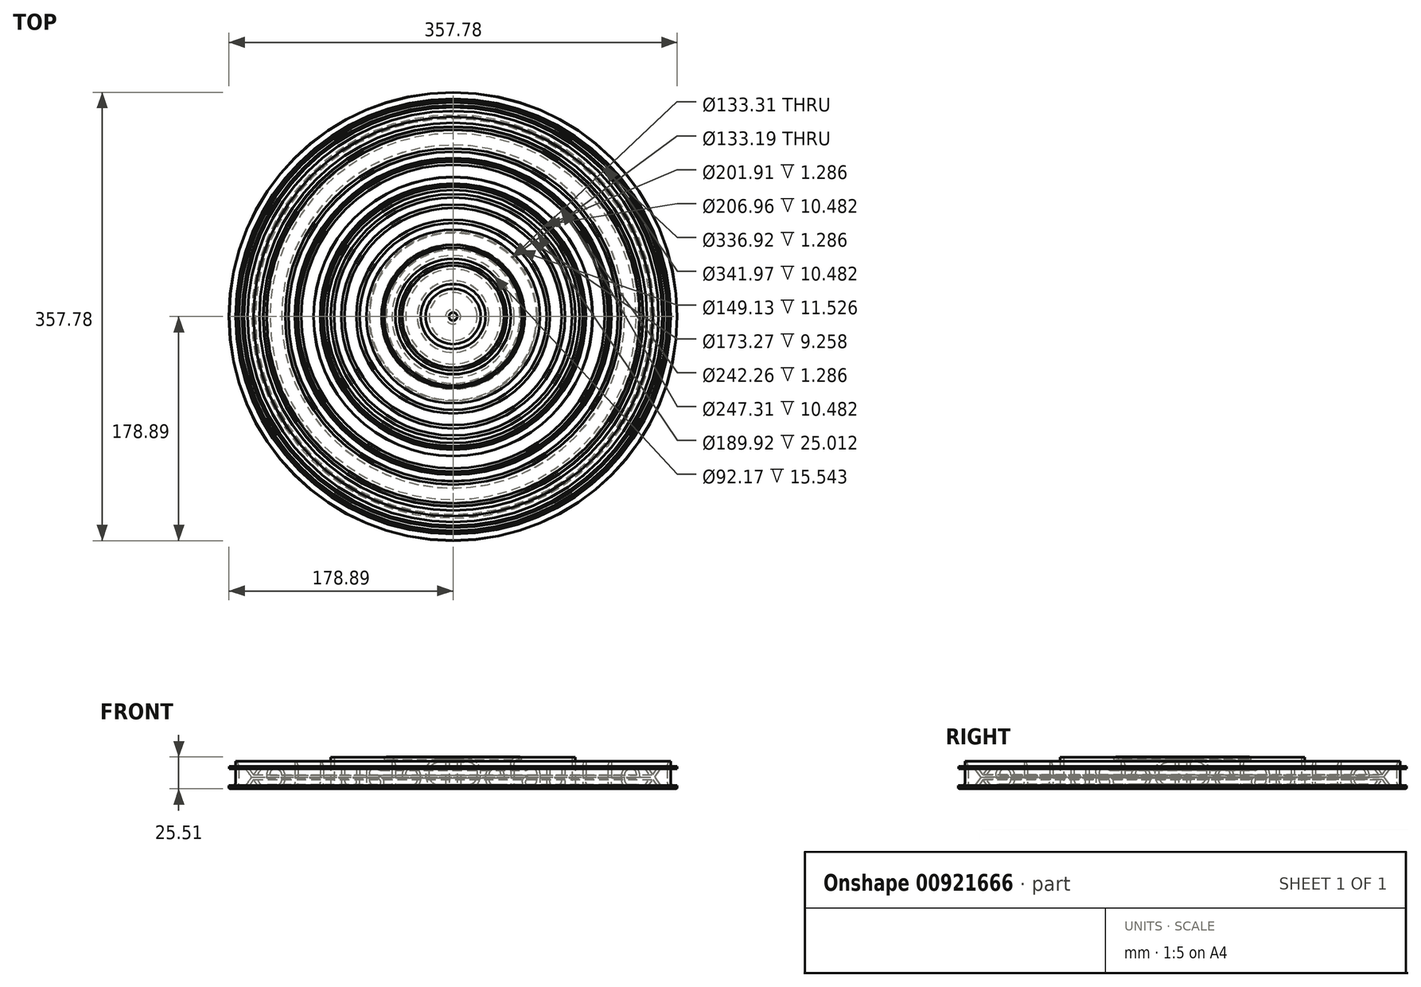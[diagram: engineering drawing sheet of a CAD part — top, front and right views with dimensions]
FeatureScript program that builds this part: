
annotation { "Feature Type Name" : "Feature", "Feature Type Description" : "" }
export const myFeature = defineFeature(function(context is Context, id is Id, definition is map)
    precondition{}
    {
        {
            var Q0;
            Q0=qCreatedBy(makeId("Front.planeOp"),FACE);
            var sketch = newSketch(context, id + "F0", { "sketchPlane" : qUnion([Q0])});
            skText(sketch, "E0", { "text": "Default text", "fontName": "OpenSans-Regular.ttf"});
            const initialGuessF0  = {"E0": [0, -0.0237, 1, 0, 0.0237]};
            skSetInitialGuess(sketch, initialGuessF0);
            skSolve(sketch);
        }
        {
            var Q0;
            Q0 = qSketchRegion(id + "F0", true);
            var Q1;
            Q1=sQuery(id+"F0.wireOp",EDGE,"E0.sketch_text.left");
            revolve(context, id + "F1", {"surfaceOperationType" : NewSurfaceOperationType.NEW, "entities" : qUnion([Q0]), "axis" : qUnion([Q1]), "revolveType" : RevolveType.FULL});
        }
    });
